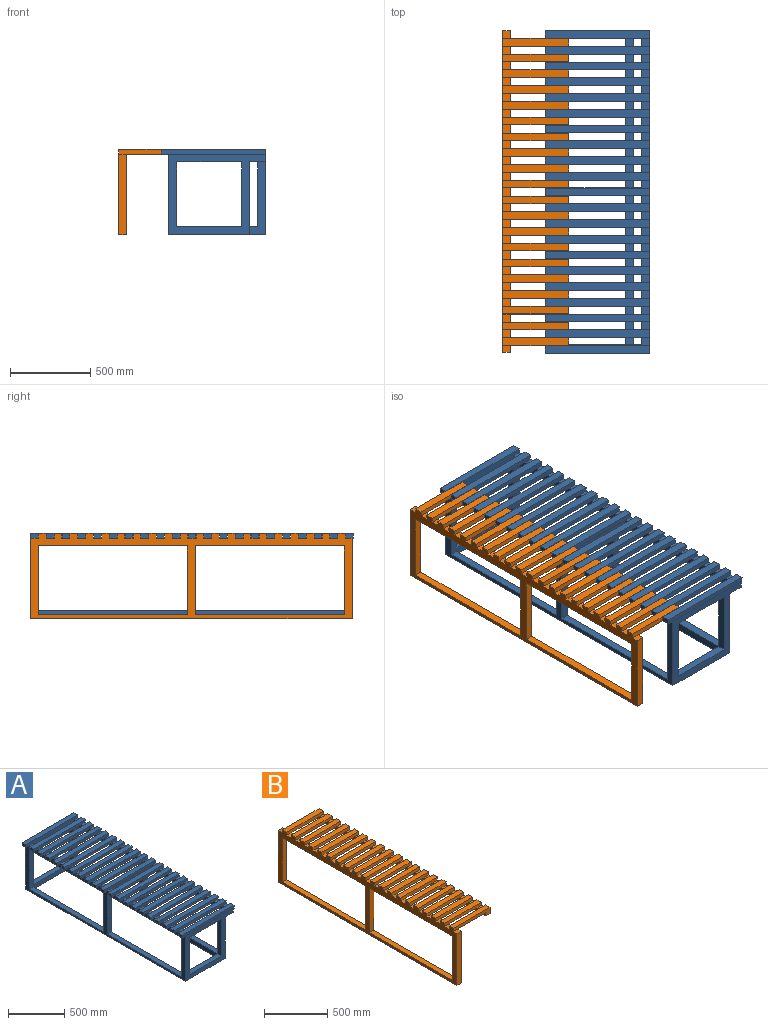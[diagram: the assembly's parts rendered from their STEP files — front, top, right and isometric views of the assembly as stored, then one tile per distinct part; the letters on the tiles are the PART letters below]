
ASSEMBLY  parts=2 mates=1
PART A: 200 faces, bbox 648x2008x528 mm
  f0: plane 976x504mm, normal (0,0,1), area 68736mm2, adj f51,f52,f55,f59,f67,f68,f71,f154
  f1: plane 452x50mm, normal (0,0,1), area 4016mm2, adj f5,f54,f58,f106,f154,f158
  f2: plane 100x50mm, normal (0,0,1), area 2608mm2, adj f5,f8,f64,f106,f154,f157
  f3: plane 404x48mm, normal (0,0,-1), area 19392mm2, adj f6,f68,f154,f155
  f4: plane 1952x100mm, normal (0,0,-1), area 98688mm2, adj f8,f52,f60,f64,f65,f67,f70,f154
  f5: plane 648x30mm, normal (0,1,0), area 19344mm2, adj f1,f2,f64,f110,f156,f157,f158,f179
  f6: plane 1904x450mm, normal (1,0,0), area 64288mm2, adj f3,f10,f51,f57,f61,f62,f152,f153
  f7: plane 928x48mm, normal (1,0,0), area 44544mm2, adj f9,f11,f13,f15,f17,f19,f21,f23
  f8: plane 928x48mm, normal (-1,0,0), area 44544mm2, adj f2,f4,f30,f32,f34,f36,f38,f40
  f9: plane 928x48mm, normal (0,0,-1), area 44544mm2, adj f7,f57,f58,f152
  f10: plane 928x48mm, normal (0,0,1), area 44544mm2, adj f6,f51,f58,f153
  f11: plane 600x50mm, normal (0,0,1), area 8832mm2, adj f7,f58,f64,f65,f70,f145,f149
  f12: plane 50x48mm, normal (0,0,1), area 2400mm2, adj f64,f70,f141,f144
  f13: plane 50x48mm, normal (0,0,1), area 2400mm2, adj f7,f58,f141,f144
  f14: plane 50x48mm, normal (0,0,1), area 2400mm2, adj f64,f70,f137,f140
  f15: plane 50x48mm, normal (0,0,1), area 2400mm2, adj f7,f58,f137,f140
  f16: plane 50x48mm, normal (0,0,1), area 2400mm2, adj f64,f70,f133,f136
  f17: plane 50x48mm, normal (0,0,1), area 2400mm2, adj f7,f58,f133,f136
  f18: plane 50x48mm, normal (0,0,1), area 2400mm2, adj f64,f70,f129,f132
  f19: plane 50x48mm, normal (0,0,1), area 2400mm2, adj f7,f58,f129,f132
  f20: plane 50x48mm, normal (0,0,1), area 2400mm2, adj f64,f70,f125,f128
  f21: plane 50x48mm, normal (0,0,1), area 2400mm2, adj f7,f58,f125,f128
  f22: plane 50x48mm, normal (0,0,1), area 2400mm2, adj f64,f70,f121,f124
  f23: plane 50x48mm, normal (0,0,1), area 2400mm2, adj f7,f58,f121,f124
  f24: plane 50x48mm, normal (0,0,1), area 2400mm2, adj f64,f70,f117,f120
  f25: plane 50x48mm, normal (0,0,1), area 2400mm2, adj f7,f58,f117,f120
  f26: plane 50x48mm, normal (0,0,1), area 2400mm2, adj f64,f70,f113,f116
  f27: plane 50x48mm, normal (0,0,1), area 2400mm2, adj f7,f58,f113,f116
  f28: plane 50x48mm, normal (0,0,1), area 2400mm2, adj f64,f70,f109,f112
  f29: plane 50x48mm, normal (0,0,1), area 2400mm2, adj f7,f58,f109,f112
  f30: plane 50x48mm, normal (0,0,1), area 2400mm2, adj f8,f64,f102,f105
  f31: plane 50x48mm, normal (0,0,1), area 2400mm2, adj f54,f58,f102,f105
  f32: plane 50x48mm, normal (0,0,1), area 2400mm2, adj f8,f64,f98,f101
  f33: plane 50x48mm, normal (0,0,1), area 2400mm2, adj f54,f58,f98,f101
  f34: plane 50x48mm, normal (0,0,1), area 2400mm2, adj f8,f64,f94,f97
  f35: plane 50x48mm, normal (0,0,1), area 2400mm2, adj f54,f58,f94,f97
  f36: plane 50x48mm, normal (0,0,1), area 2400mm2, adj f8,f64,f90,f93
  f37: plane 50x48mm, normal (0,0,1), area 2400mm2, adj f54,f58,f90,f93
  f38: plane 50x48mm, normal (0,0,1), area 2400mm2, adj f8,f64,f86,f89
  f39: plane 50x48mm, normal (0,0,1), area 2400mm2, adj f54,f58,f86,f89
  f40: plane 50x48mm, normal (0,0,1), area 2400mm2, adj f8,f64,f82,f85
  f41: plane 50x48mm, normal (0,0,1), area 2400mm2, adj f54,f58,f82,f85
  f42: plane 50x48mm, normal (0,0,1), area 2400mm2, adj f8,f64,f78,f81
  f43: plane 50x48mm, normal (0,0,1), area 2400mm2, adj f54,f58,f78,f81
  f44: plane 50x48mm, normal (0,0,1), area 2400mm2, adj f8,f64,f74,f77
  f45: plane 50x48mm, normal (0,0,1), area 2400mm2, adj f54,f58,f74,f77
  f46: plane 50x48mm, normal (0,0,1), area 2400mm2, adj f8,f63,f64,f73
  f47: plane 50x48mm, normal (0,0,1), area 2400mm2, adj f54,f58,f63,f73
  f48: plane 928x48mm, normal (0,0,1), area 44544mm2, adj f65,f67,f68,f155
  f49: plane 504x48mm, normal (0,0,-1), area 24192mm2, adj f55,f59,f63,f71
  f50: plane 404x48mm, normal (0,0,1), area 19392mm2, adj f53,f57,f60,f69
  f51: plane 452x450mm, normal (0,-1,0), area 39888mm2, adj f0,f6,f10,f55,f56,f58,f61,f68
  f52: plane 450x100mm, normal (0,-1,0), area 24096mm2, adj f0,f4,f61,f64,f67,f71
  f53: plane 402x48mm, normal (1,0,0), area 19296mm2, adj f50,f57,f60,f66
  f54: plane 928x48mm, normal (1,0,0), area 44544mm2, adj f1,f31,f33,f35,f37,f39,f41,f43
  f55: plane 402x48mm, normal (1,0,0), area 19296mm2, adj f0,f49,f51,f59
  f56: plane 928x48mm, normal (0,0,-1), area 44544mm2, adj f51,f54,f58,f153
  f57: plane 452x450mm, normal (0,1,0), area 39888mm2, adj f6,f9,f50,f53,f58,f61,f62,f68
  f58: plane 2000x498mm, normal (-1,0,0), area 203488mm2, adj f1,f9,f10,f11,f13,f15,f17,f19
  f59: plane 648x528mm, normal (0,1,0), area 115632mm2, adj f0,f49,f55,f58,f61,f64,f71,f72
  f60: plane 600x498mm, normal (0,-1,0), area 91392mm2, adj f4,f50,f53,f58,f61,f64,f66,f67
  f61: plane 2000x600mm, normal (0,0,-1), area 235584mm2, adj f6,f51,f52,f57,f58,f59,f60,f64
  f62: plane 928x48mm, normal (0,0,1), area 44544mm2, adj f6,f57,f58,f152
  f63: plane 648x78mm, normal (0,-1,0), area 43632mm2, adj f8,f46,f47,f49,f54,f64,f72,f159
  f64: plane 2008x528mm, normal (1,0,0), area 147840mm2, adj f2,f4,f5,f11,f12,f14,f16,f18
  f65: plane 504x450mm, normal (0,1,0), area 43488mm2, adj f4,f7,f11,f48,f66,f67,f69,f70
  f66: plane 404x48mm, normal (0,0,-1), area 19392mm2, adj f53,f60,f65,f69
  f67: plane 1952x450mm, normal (1,0,0), area 132288mm2, adj f0,f4,f48,f52,f60,f61,f65,f154
  f68: plane 1904x450mm, normal (-1,0,0), area 110688mm2, adj f0,f3,f48,f51,f57,f61,f154,f155
  f69: plane 402x48mm, normal (-1,0,0), area 19296mm2, adj f50,f60,f65,f66
  f70: plane 928x48mm, normal (-1,0,0), area 44544mm2, adj f4,f11,f12,f14,f16,f18,f20,f22
  f71: plane 402x48mm, normal (-1,0,0), area 19296mm2, adj f0,f49,f52,f59
  f72: plane 648x48mm, normal (0,0,1), area 31104mm2, adj f59,f63,f64,f160
  f73: plane 648x30mm, normal (0,1,0), area 19440mm2, adj f46,f47,f64,f75,f76,f161,f162
  f74: plane 648x30mm, normal (0,-1,0), area 19440mm2, adj f44,f45,f64,f75,f76,f161,f162
  f75: plane 648x48mm, normal (0,0,1), area 31104mm2, adj f64,f73,f74,f162
  f76: plane 504x48mm, normal (0,0,-1), area 24192mm2, adj f8,f54,f73,f74
  f77: plane 648x30mm, normal (0,1,0), area 19440mm2, adj f44,f45,f64,f79,f80,f163,f164
  f78: plane 648x30mm, normal (0,-1,0), area 19440mm2, adj f42,f43,f64,f79,f80,f163,f164
  f79: plane 648x48mm, normal (0,0,1), area 31104mm2, adj f64,f77,f78,f164
  f80: plane 504x48mm, normal (0,0,-1), area 24192mm2, adj f8,f54,f77,f78
  f81: plane 648x30mm, normal (0,1,0), area 19440mm2, adj f42,f43,f64,f83,f84,f165,f166
  f82: plane 648x30mm, normal (0,-1,0), area 19440mm2, adj f40,f41,f64,f83,f84,f165,f166
  f83: plane 648x48mm, normal (0,0,1), area 31104mm2, adj f64,f81,f82,f166
  f84: plane 504x48mm, normal (0,0,-1), area 24192mm2, adj f8,f54,f81,f82
  f85: plane 648x30mm, normal (0,1,0), area 19440mm2, adj f40,f41,f64,f87,f88,f167,f168
  f86: plane 648x30mm, normal (0,-1,0), area 19440mm2, adj f38,f39,f64,f87,f88,f167,f168
  f87: plane 648x48mm, normal (0,0,1), area 31104mm2, adj f64,f85,f86,f168
  f88: plane 504x48mm, normal (0,0,-1), area 24192mm2, adj f8,f54,f85,f86
  f89: plane 648x30mm, normal (0,1,0), area 19440mm2, adj f38,f39,f64,f91,f92,f169,f170
  f90: plane 648x30mm, normal (0,-1,0), area 19440mm2, adj f36,f37,f64,f91,f92,f169,f170
  f91: plane 648x48mm, normal (0,0,1), area 31104mm2, adj f64,f89,f90,f170
  f92: plane 504x48mm, normal (0,0,-1), area 24192mm2, adj f8,f54,f89,f90
  f93: plane 648x30mm, normal (0,1,0), area 19440mm2, adj f36,f37,f64,f95,f96,f171,f172
  f94: plane 648x30mm, normal (0,-1,0), area 19440mm2, adj f34,f35,f64,f95,f96,f171,f172
  f95: plane 648x48mm, normal (0,0,1), area 31104mm2, adj f64,f93,f94,f172
  f96: plane 504x48mm, normal (0,0,-1), area 24192mm2, adj f8,f54,f93,f94
  f97: plane 648x30mm, normal (0,1,0), area 19440mm2, adj f34,f35,f64,f99,f100,f173,f174
  f98: plane 648x30mm, normal (0,-1,0), area 19440mm2, adj f32,f33,f64,f99,f100,f173,f174
  f99: plane 648x48mm, normal (0,0,1), area 31104mm2, adj f64,f97,f98,f174
  f100: plane 504x48mm, normal (0,0,-1), area 24192mm2, adj f8,f54,f97,f98
  f101: plane 648x30mm, normal (0,1,0), area 19440mm2, adj f32,f33,f64,f103,f104,f175,f176
  f102: plane 648x30mm, normal (0,-1,0), area 19440mm2, adj f30,f31,f64,f103,f104,f175,f176
  f103: plane 648x48mm, normal (0,0,1), area 31104mm2, adj f64,f101,f102,f176
  f104: plane 504x48mm, normal (0,0,-1), area 24192mm2, adj f8,f54,f101,f102
  f105: plane 648x30mm, normal (0,1,0), area 19440mm2, adj f30,f31,f64,f107,f108,f177,f178
  f106: plane 648x30mm, normal (0,-1,0), area 19440mm2, adj f1,f2,f64,f107,f108,f177,f178
  f107: plane 648x48mm, normal (0,0,1), area 31104mm2, adj f64,f105,f106,f178
  f108: plane 504x48mm, normal (0,0,-1), area 24192mm2, adj f8,f54,f105,f106
  f109: plane 648x30mm, normal (0,-1,0), area 19440mm2, adj f28,f29,f64,f110,f111,f179,f180
  f110: plane 648x48mm, normal (0,0,1), area 31104mm2, adj f5,f64,f109,f180
  f111: plane 504x4mm, normal (0,0,-1), area 2016mm2, adj f7,f70,f109,f155
  f112: plane 648x30mm, normal (0,1,0), area 19440mm2, adj f28,f29,f64,f114,f115,f181,f182
  f113: plane 648x30mm, normal (0,-1,0), area 19440mm2, adj f26,f27,f64,f114,f115,f181,f182
  f114: plane 648x48mm, normal (0,0,1), area 31104mm2, adj f64,f112,f113,f182
  f115: plane 504x48mm, normal (0,0,-1), area 24192mm2, adj f7,f70,f112,f113
  f116: plane 648x30mm, normal (0,1,0), area 19440mm2, adj f26,f27,f64,f118,f119,f183,f184
  f117: plane 648x30mm, normal (0,-1,0), area 19440mm2, adj f24,f25,f64,f118,f119,f183,f184
  f118: plane 648x48mm, normal (0,0,1), area 31104mm2, adj f64,f116,f117,f184
  f119: plane 504x48mm, normal (0,0,-1), area 24192mm2, adj f7,f70,f116,f117
  f120: plane 648x30mm, normal (0,1,0), area 19440mm2, adj f24,f25,f64,f122,f123,f185,f186
  f121: plane 648x30mm, normal (0,-1,0), area 19440mm2, adj f22,f23,f64,f122,f123,f185,f186
  f122: plane 648x48mm, normal (0,0,1), area 31104mm2, adj f64,f120,f121,f186
  f123: plane 504x48mm, normal (0,0,-1), area 24192mm2, adj f7,f70,f120,f121
  f124: plane 648x30mm, normal (0,1,0), area 19440mm2, adj f22,f23,f64,f126,f127,f187,f188
  f125: plane 648x30mm, normal (0,-1,0), area 19440mm2, adj f20,f21,f64,f126,f127,f187,f188
  f126: plane 648x48mm, normal (0,0,1), area 31104mm2, adj f64,f124,f125,f188
  f127: plane 504x48mm, normal (0,0,-1), area 24192mm2, adj f7,f70,f124,f125
  f128: plane 648x30mm, normal (0,1,0), area 19440mm2, adj f20,f21,f64,f130,f131,f189,f190
  f129: plane 648x30mm, normal (0,-1,0), area 19440mm2, adj f18,f19,f64,f130,f131,f189,f190
  f130: plane 648x48mm, normal (0,0,1), area 31104mm2, adj f64,f128,f129,f190
  f131: plane 504x48mm, normal (0,0,-1), area 24192mm2, adj f7,f70,f128,f129
  f132: plane 648x30mm, normal (0,1,0), area 19440mm2, adj f18,f19,f64,f134,f135,f191,f192
  f133: plane 648x30mm, normal (0,-1,0), area 19440mm2, adj f16,f17,f64,f134,f135,f191,f192
  f134: plane 648x48mm, normal (0,0,1), area 31104mm2, adj f64,f132,f133,f192
  f135: plane 504x48mm, normal (0,0,-1), area 24192mm2, adj f7,f70,f132,f133
  f136: plane 648x30mm, normal (0,1,0), area 19440mm2, adj f16,f17,f64,f138,f139,f193,f194
  f137: plane 648x30mm, normal (0,-1,0), area 19440mm2, adj f14,f15,f64,f138,f139,f193,f194
  f138: plane 648x48mm, normal (0,0,1), area 31104mm2, adj f64,f136,f137,f194
  f139: plane 504x48mm, normal (0,0,-1), area 24192mm2, adj f7,f70,f136,f137
  f140: plane 648x30mm, normal (0,1,0), area 19440mm2, adj f14,f15,f64,f142,f143,f195,f196
  f141: plane 648x30mm, normal (0,-1,0), area 19440mm2, adj f12,f13,f64,f142,f143,f195,f196
  f142: plane 648x48mm, normal (0,0,1), area 31104mm2, adj f64,f140,f141,f196
  f143: plane 504x48mm, normal (0,0,-1), area 24192mm2, adj f7,f70,f140,f141
  f144: plane 648x30mm, normal (0,1,0), area 19440mm2, adj f12,f13,f64,f146,f147,f197,f198
  f145: plane 648x30mm, normal (0,-1,0), area 19440mm2, adj f11,f64,f146,f147,f197,f198
  f146: plane 648x48mm, normal (0,0,1), area 31104mm2, adj f64,f144,f145,f198
  f147: plane 504x48mm, normal (0,0,-1), area 24192mm2, adj f7,f70,f144,f145
  f148: plane 648x48mm, normal (0,0,-1), area 7104mm2, adj f58,f60,f64,f149,f150,f199
  f149: plane 648x30mm, normal (0,1,0), area 19440mm2, adj f11,f64,f148,f151,f199
  f150: plane 648x30mm, normal (0,-1,0), area 19440mm2, adj f64,f148,f151,f199
  f151: plane 648x48mm, normal (0,0,1), area 31104mm2, adj f64,f149,f150,f199
  f152: plane 427x48mm, normal (0,-1,0), area 20496mm2, adj f6,f9,f58,f62
  f153: plane 427x48mm, normal (0,1,0), area 20496mm2, adj f6,f10,f56,f58
  f154: plane 504x452mm, normal (0,1,0), area 43584mm2, adj f0,f1,f2,f3,f4,f8,f54,f67
  f155: plane 504x450mm, normal (0,-1,0), area 43488mm2, adj f3,f4,f7,f48,f67,f68,f70,f111
  f156: plane 48x4mm, normal (0,0,1), area 192mm2, adj f5,f154,f157,f158
  f157: plane 4x2mm, normal (1,0,0), area 8mm2, adj f2,f5,f154,f156
  f158: plane 4x2mm, normal (-1,0,0), area 8mm2, adj f1,f5,f154,f156
  f159: plane 48x48mm, normal (0,0,-1), area 2304mm2, adj f58,f59,f63,f160
  f160: plane 48x30mm, normal (-1,0,0), area 1440mm2, adj f59,f63,f72,f159
  f161: plane 48x48mm, normal (0,0,-1), area 2304mm2, adj f58,f73,f74,f162
  f162: plane 48x30mm, normal (-1,0,0), area 1440mm2, adj f73,f74,f75,f161
  f163: plane 48x48mm, normal (0,0,-1), area 2304mm2, adj f58,f77,f78,f164
  f164: plane 48x30mm, normal (-1,0,0), area 1440mm2, adj f77,f78,f79,f163
  f165: plane 48x48mm, normal (0,0,-1), area 2304mm2, adj f58,f81,f82,f166
  f166: plane 48x30mm, normal (-1,0,0), area 1440mm2, adj f81,f82,f83,f165
  f167: plane 48x48mm, normal (0,0,-1), area 2304mm2, adj f58,f85,f86,f168
  f168: plane 48x30mm, normal (-1,0,0), area 1440mm2, adj f85,f86,f87,f167
  f169: plane 48x48mm, normal (0,0,-1), area 2304mm2, adj f58,f89,f90,f170
  f170: plane 48x30mm, normal (-1,0,0), area 1440mm2, adj f89,f90,f91,f169
  f171: plane 48x48mm, normal (0,0,-1), area 2304mm2, adj f58,f93,f94,f172
  f172: plane 48x30mm, normal (-1,0,0), area 1440mm2, adj f93,f94,f95,f171
  f173: plane 48x48mm, normal (0,0,-1), area 2304mm2, adj f58,f97,f98,f174
  f174: plane 48x30mm, normal (-1,0,0), area 1440mm2, adj f97,f98,f99,f173
  f175: plane 48x48mm, normal (0,0,-1), area 2304mm2, adj f58,f101,f102,f176
  f176: plane 48x30mm, normal (-1,0,0), area 1440mm2, adj f101,f102,f103,f175
  f177: plane 48x48mm, normal (0,0,-1), area 2304mm2, adj f58,f105,f106,f178
  f178: plane 48x30mm, normal (-1,0,0), area 1440mm2, adj f105,f106,f107,f177
  f179: plane 48x48mm, normal (0,0,-1), area 2304mm2, adj f5,f58,f109,f180
  f180: plane 48x30mm, normal (-1,0,0), area 1440mm2, adj f5,f109,f110,f179
  f181: plane 48x48mm, normal (0,0,-1), area 2304mm2, adj f58,f112,f113,f182
  f182: plane 48x30mm, normal (-1,0,0), area 1440mm2, adj f112,f113,f114,f181
  f183: plane 48x48mm, normal (0,0,-1), area 2304mm2, adj f58,f116,f117,f184
  f184: plane 48x30mm, normal (-1,0,0), area 1440mm2, adj f116,f117,f118,f183
  f185: plane 48x48mm, normal (0,0,-1), area 2304mm2, adj f58,f120,f121,f186
  f186: plane 48x30mm, normal (-1,0,0), area 1440mm2, adj f120,f121,f122,f185
  f187: plane 48x48mm, normal (0,0,-1), area 2304mm2, adj f58,f124,f125,f188
  f188: plane 48x30mm, normal (-1,0,0), area 1440mm2, adj f124,f125,f126,f187
  f189: plane 48x48mm, normal (0,0,-1), area 2304mm2, adj f58,f128,f129,f190
  f190: plane 48x30mm, normal (-1,0,0), area 1440mm2, adj f128,f129,f130,f189
  f191: plane 48x48mm, normal (0,0,-1), area 2304mm2, adj f58,f132,f133,f192
  f192: plane 48x30mm, normal (-1,0,0), area 1440mm2, adj f132,f133,f134,f191
  f193: plane 48x48mm, normal (0,0,-1), area 2304mm2, adj f58,f136,f137,f194
  f194: plane 48x30mm, normal (-1,0,0), area 1440mm2, adj f136,f137,f138,f193
  f195: plane 48x48mm, normal (0,0,-1), area 2304mm2, adj f58,f140,f141,f196
  f196: plane 48x30mm, normal (-1,0,0), area 1440mm2, adj f140,f141,f142,f195
  f197: plane 48x48mm, normal (0,0,-1), area 2304mm2, adj f58,f144,f145,f198
  f198: plane 48x30mm, normal (-1,0,0), area 1440mm2, adj f144,f145,f146,f197
  f199: plane 48x30mm, normal (-1,0,0), area 1440mm2, adj f148,f149,f150,f151
PART B: 136 faces, bbox 410x2000x530 mm
  f0: plane 314x48mm, normal (0,0,-1), area 15072mm2, adj f34,f35,f36,f115
  f1: plane 48x41mm, normal (0,0,1), area 1968mm2, adj f32,f33,f34,f111
  f2: plane 50x48mm, normal (0,0,1), area 2400mm2, adj f33,f34,f107,f112
  f3: plane 50x48mm, normal (0,0,1), area 2400mm2, adj f33,f34,f103,f108
  f4: plane 50x48mm, normal (0,0,1), area 2400mm2, adj f33,f34,f99,f104
  f5: plane 50x48mm, normal (0,0,1), area 2400mm2, adj f33,f34,f95,f100
  f6: plane 50x48mm, normal (0,0,1), area 2400mm2, adj f33,f34,f91,f96
  f7: plane 50x48mm, normal (0,0,1), area 2400mm2, adj f33,f34,f87,f92
  f8: plane 50x48mm, normal (0,0,1), area 2400mm2, adj f33,f34,f83,f88
  f9: plane 50x48mm, normal (0,0,1), area 2400mm2, adj f33,f34,f79,f84
  f10: plane 50x48mm, normal (0,0,1), area 2400mm2, adj f33,f34,f75,f80
  f11: plane 50x48mm, normal (0,0,1), area 2400mm2, adj f33,f34,f71,f76
  f12: plane 50x48mm, normal (0,0,1), area 2400mm2, adj f33,f34,f67,f72
  f13: plane 50x48mm, normal (0,0,1), area 2400mm2, adj f33,f34,f63,f68
  f14: plane 50x48mm, normal (0,0,1), area 2400mm2, adj f33,f34,f59,f64
  f15: plane 50x48mm, normal (0,0,1), area 2400mm2, adj f33,f34,f55,f60
  f16: plane 50x48mm, normal (0,0,1), area 2400mm2, adj f33,f34,f51,f56
  f17: plane 50x48mm, normal (0,0,1), area 2400mm2, adj f33,f34,f47,f52
  f18: plane 50x48mm, normal (0,0,1), area 2400mm2, adj f33,f34,f43,f48
  f19: plane 50x48mm, normal (0,0,1), area 2400mm2, adj f33,f34,f39,f44
  f20: plane 50x48mm, normal (0,0,1), area 2400mm2, adj f33,f34,f35,f40
  f21: plane 49x48mm, normal (0,0,1), area 2352mm2, adj f23,f33,f34,f36
  f22: plane 2000x48mm, normal (0,0,-1), area 96000mm2, adj f23,f32,f33,f34
  f23: plane 500x48mm, normal (0,1,0), area 24000mm2, adj f21,f22,f33,f34
  f24: plane 928x48mm, normal (0,0,-1), area 44544mm2, adj f25,f30,f33,f34
  f25: plane 429x48mm, normal (0,-1,0), area 20592mm2, adj f24,f26,f33,f34
  f26: plane 928x48mm, normal (0,0,1), area 44544mm2, adj f25,f30,f33,f34
  f27: plane 429x48mm, normal (0,-1,0), area 20592mm2, adj f28,f31,f33,f34
  f28: plane 928x48mm, normal (0,0,1), area 44544mm2, adj f27,f29,f33,f34
  f29: plane 429x48mm, normal (0,1,0), area 20592mm2, adj f28,f31,f33,f34
  f30: plane 429x48mm, normal (0,1,0), area 20592mm2, adj f24,f26,f33,f34
  f31: plane 928x48mm, normal (0,0,-1), area 44544mm2, adj f27,f29,f33,f34
  f32: plane 500x48mm, normal (0,-1,0), area 24000mm2, adj f1,f22,f33,f34
  f33: plane 2000x530mm, normal (-1,0,0), area 232576mm2, adj f1,f2,f3,f4,f5,f6,f7,f8
  f34: plane 2000x500mm, normal (1,0,0), area 203776mm2, adj f0,f1,f2,f3,f4,f5,f6,f7
  f35: plane 410x30mm, normal (0,-1,0), area 12300mm2, adj f0,f20,f33,f37,f38,f117
  f36: plane 410x60mm, normal (0,1,0), area 13740mm2, adj f0,f21,f33,f37,f38,f115,f116
  f37: plane 410x48mm, normal (0,0,1), area 19680mm2, adj f33,f35,f36,f38
  f38: plane 1910x60mm, normal (1,0,0), area 86100mm2, adj f35,f36,f37,f39,f40,f41,f43,f44
  f39: plane 410x30mm, normal (0,-1,0), area 12300mm2, adj f19,f33,f38,f41,f42,f118
  f40: plane 410x30mm, normal (0,1,0), area 12300mm2, adj f20,f33,f38,f41,f42,f117
  f41: plane 410x48mm, normal (0,0,1), area 19680mm2, adj f33,f38,f39,f40
  f42: plane 314x48mm, normal (0,0,-1), area 15072mm2, adj f34,f39,f40,f115
  f43: plane 410x30mm, normal (0,-1,0), area 12300mm2, adj f18,f33,f38,f45,f46,f119
  f44: plane 410x30mm, normal (0,1,0), area 12300mm2, adj f19,f33,f38,f45,f46,f118
  f45: plane 410x48mm, normal (0,0,1), area 19680mm2, adj f33,f38,f43,f44
  f46: plane 314x48mm, normal (0,0,-1), area 15072mm2, adj f34,f43,f44,f115
  f47: plane 410x30mm, normal (0,-1,0), area 12300mm2, adj f17,f33,f38,f49,f50,f120
  f48: plane 410x30mm, normal (0,1,0), area 12300mm2, adj f18,f33,f38,f49,f50,f119
  f49: plane 410x48mm, normal (0,0,1), area 19680mm2, adj f33,f38,f47,f48
  f50: plane 314x48mm, normal (0,0,-1), area 15072mm2, adj f34,f47,f48,f115
  f51: plane 410x30mm, normal (0,-1,0), area 12300mm2, adj f16,f33,f38,f53,f54,f121
  f52: plane 410x30mm, normal (0,1,0), area 12300mm2, adj f17,f33,f38,f53,f54,f120
  f53: plane 410x48mm, normal (0,0,1), area 19680mm2, adj f33,f38,f51,f52
  f54: plane 314x48mm, normal (0,0,-1), area 15072mm2, adj f34,f51,f52,f115
  f55: plane 410x30mm, normal (0,-1,0), area 12300mm2, adj f15,f33,f38,f57,f58,f122
  f56: plane 410x30mm, normal (0,1,0), area 12300mm2, adj f16,f33,f38,f57,f58,f121
  f57: plane 410x48mm, normal (0,0,1), area 19680mm2, adj f33,f38,f55,f56
  f58: plane 314x48mm, normal (0,0,-1), area 15072mm2, adj f34,f55,f56,f115
  f59: plane 410x30mm, normal (0,-1,0), area 12300mm2, adj f14,f33,f38,f61,f62,f123
  f60: plane 410x30mm, normal (0,1,0), area 12300mm2, adj f15,f33,f38,f61,f62,f122
  f61: plane 410x48mm, normal (0,0,1), area 19680mm2, adj f33,f38,f59,f60
  f62: plane 314x48mm, normal (0,0,-1), area 15072mm2, adj f34,f59,f60,f115
  f63: plane 410x30mm, normal (0,-1,0), area 12300mm2, adj f13,f33,f38,f65,f66,f124
  f64: plane 410x30mm, normal (0,1,0), area 12300mm2, adj f14,f33,f38,f65,f66,f123
  f65: plane 410x48mm, normal (0,0,1), area 19680mm2, adj f33,f38,f63,f64
  f66: plane 314x48mm, normal (0,0,-1), area 15072mm2, adj f34,f63,f64,f115
  f67: plane 410x30mm, normal (0,-1,0), area 12300mm2, adj f12,f33,f38,f69,f70,f125
  f68: plane 410x30mm, normal (0,1,0), area 12300mm2, adj f13,f33,f38,f69,f70,f124
  f69: plane 410x48mm, normal (0,0,1), area 19680mm2, adj f33,f38,f67,f68
  f70: plane 314x48mm, normal (0,0,-1), area 15072mm2, adj f34,f67,f68,f115
  f71: plane 410x30mm, normal (0,-1,0), area 12300mm2, adj f11,f33,f38,f73,f74,f126
  f72: plane 410x30mm, normal (0,1,0), area 12300mm2, adj f12,f33,f38,f73,f74,f125
  f73: plane 410x48mm, normal (0,0,1), area 19680mm2, adj f33,f38,f71,f72
  f74: plane 314x48mm, normal (0,0,-1), area 15072mm2, adj f34,f71,f72,f115
  f75: plane 410x30mm, normal (0,-1,0), area 12300mm2, adj f10,f33,f38,f77,f78,f127
  f76: plane 410x30mm, normal (0,1,0), area 12300mm2, adj f11,f33,f38,f77,f78,f126
  f77: plane 410x48mm, normal (0,0,1), area 19680mm2, adj f33,f38,f75,f76
  f78: plane 314x48mm, normal (0,0,-1), area 15072mm2, adj f34,f75,f76,f115
  f79: plane 410x30mm, normal (0,-1,0), area 12300mm2, adj f9,f33,f38,f81,f82,f128
  f80: plane 410x30mm, normal (0,1,0), area 12300mm2, adj f10,f33,f38,f81,f82,f127
  f81: plane 410x48mm, normal (0,0,1), area 19680mm2, adj f33,f38,f79,f80
  f82: plane 314x48mm, normal (0,0,-1), area 15072mm2, adj f34,f79,f80,f115
  f83: plane 410x30mm, normal (0,-1,0), area 12300mm2, adj f8,f33,f38,f85,f86,f129
  f84: plane 410x30mm, normal (0,1,0), area 12300mm2, adj f9,f33,f38,f85,f86,f128
  f85: plane 410x48mm, normal (0,0,1), area 19680mm2, adj f33,f38,f83,f84
  f86: plane 314x48mm, normal (0,0,-1), area 15072mm2, adj f34,f83,f84,f115
  f87: plane 410x30mm, normal (0,-1,0), area 12300mm2, adj f7,f33,f38,f89,f90,f130
  f88: plane 410x30mm, normal (0,1,0), area 12300mm2, adj f8,f33,f38,f89,f90,f129
  f89: plane 410x48mm, normal (0,0,1), area 19680mm2, adj f33,f38,f87,f88
  f90: plane 314x48mm, normal (0,0,-1), area 15072mm2, adj f34,f87,f88,f115
  f91: plane 410x30mm, normal (0,-1,0), area 12300mm2, adj f6,f33,f38,f93,f94,f131
  f92: plane 410x30mm, normal (0,1,0), area 12300mm2, adj f7,f33,f38,f93,f94,f130
  f93: plane 410x48mm, normal (0,0,1), area 19680mm2, adj f33,f38,f91,f92
  f94: plane 314x48mm, normal (0,0,-1), area 15072mm2, adj f34,f91,f92,f115
  f95: plane 410x30mm, normal (0,-1,0), area 12300mm2, adj f5,f33,f38,f97,f98,f132
  f96: plane 410x30mm, normal (0,1,0), area 12300mm2, adj f6,f33,f38,f97,f98,f131
  f97: plane 410x48mm, normal (0,0,1), area 19680mm2, adj f33,f38,f95,f96
  f98: plane 314x48mm, normal (0,0,-1), area 15072mm2, adj f34,f95,f96,f115
  f99: plane 410x30mm, normal (0,-1,0), area 12300mm2, adj f4,f33,f38,f101,f102,f133
  f100: plane 410x30mm, normal (0,1,0), area 12300mm2, adj f5,f33,f38,f101,f102,f132
  f101: plane 410x48mm, normal (0,0,1), area 19680mm2, adj f33,f38,f99,f100
  f102: plane 314x48mm, normal (0,0,-1), area 15072mm2, adj f34,f99,f100,f115
  f103: plane 410x30mm, normal (0,-1,0), area 12300mm2, adj f3,f33,f38,f105,f106,f134
  f104: plane 410x30mm, normal (0,1,0), area 12300mm2, adj f4,f33,f38,f105,f106,f133
  f105: plane 410x48mm, normal (0,0,1), area 19680mm2, adj f33,f38,f103,f104
  f106: plane 314x48mm, normal (0,0,-1), area 15072mm2, adj f34,f103,f104,f115
  f107: plane 410x30mm, normal (0,-1,0), area 12300mm2, adj f2,f33,f38,f109,f110,f135
  f108: plane 410x30mm, normal (0,1,0), area 12300mm2, adj f3,f33,f38,f109,f110,f134
  f109: plane 410x48mm, normal (0,0,1), area 19680mm2, adj f33,f38,f107,f108
  f110: plane 314x48mm, normal (0,0,-1), area 15072mm2, adj f34,f107,f108,f115
  f111: plane 410x60mm, normal (0,-1,0), area 13740mm2, adj f1,f33,f38,f113,f114,f115,f116
  f112: plane 410x30mm, normal (0,1,0), area 12300mm2, adj f2,f33,f38,f113,f114,f135
  f113: plane 410x48mm, normal (0,0,1), area 19680mm2, adj f33,f38,f111,f112
  f114: plane 314x48mm, normal (0,0,-1), area 15072mm2, adj f34,f111,f112,f115
  f115: plane 1910x30mm, normal (-1,0,0), area 57300mm2, adj f0,f36,f42,f46,f50,f54,f58,f62
  f116: plane 1910x48mm, normal (0,0,-1), area 91680mm2, adj f36,f38,f111,f115
  f117: plane 50x48mm, normal (0,0,1), area 2400mm2, adj f35,f38,f40,f115
  f118: plane 50x48mm, normal (0,0,1), area 2400mm2, adj f38,f39,f44,f115
  f119: plane 50x48mm, normal (0,0,1), area 2400mm2, adj f38,f43,f48,f115
  f120: plane 50x48mm, normal (0,0,1), area 2400mm2, adj f38,f47,f52,f115
  f121: plane 50x48mm, normal (0,0,1), area 2400mm2, adj f38,f51,f56,f115
  f122: plane 50x48mm, normal (0,0,1), area 2400mm2, adj f38,f55,f60,f115
  f123: plane 50x48mm, normal (0,0,1), area 2400mm2, adj f38,f59,f64,f115
  f124: plane 50x48mm, normal (0,0,1), area 2400mm2, adj f38,f63,f68,f115
  f125: plane 50x48mm, normal (0,0,1), area 2400mm2, adj f38,f67,f72,f115
  f126: plane 50x48mm, normal (0,0,1), area 2400mm2, adj f38,f71,f76,f115
  f127: plane 50x48mm, normal (0,0,1), area 2400mm2, adj f38,f75,f80,f115
  f128: plane 50x48mm, normal (0,0,1), area 2400mm2, adj f38,f79,f84,f115
  f129: plane 50x48mm, normal (0,0,1), area 2400mm2, adj f38,f83,f88,f115
  f130: plane 50x48mm, normal (0,0,1), area 2400mm2, adj f38,f87,f92,f115
  f131: plane 50x48mm, normal (0,0,1), area 2400mm2, adj f38,f91,f96,f115
  f132: plane 50x48mm, normal (0,0,1), area 2400mm2, adj f38,f95,f100,f115
  f133: plane 50x48mm, normal (0,0,1), area 2400mm2, adj f38,f99,f104,f115
  f134: plane 50x48mm, normal (0,0,1), area 2400mm2, adj f38,f103,f108,f115
  f135: plane 50x48mm, normal (0,0,1), area 2400mm2, adj f38,f107,f112,f115
PLACE A t=(-651,-1947.46,492.41)mm fixed
PLACE B t=(-916,237.73,489.42)mm
MATE slider B.f34 <-> A.f58  axis (1,0,0) through (-916,4.54,492.41)mm
